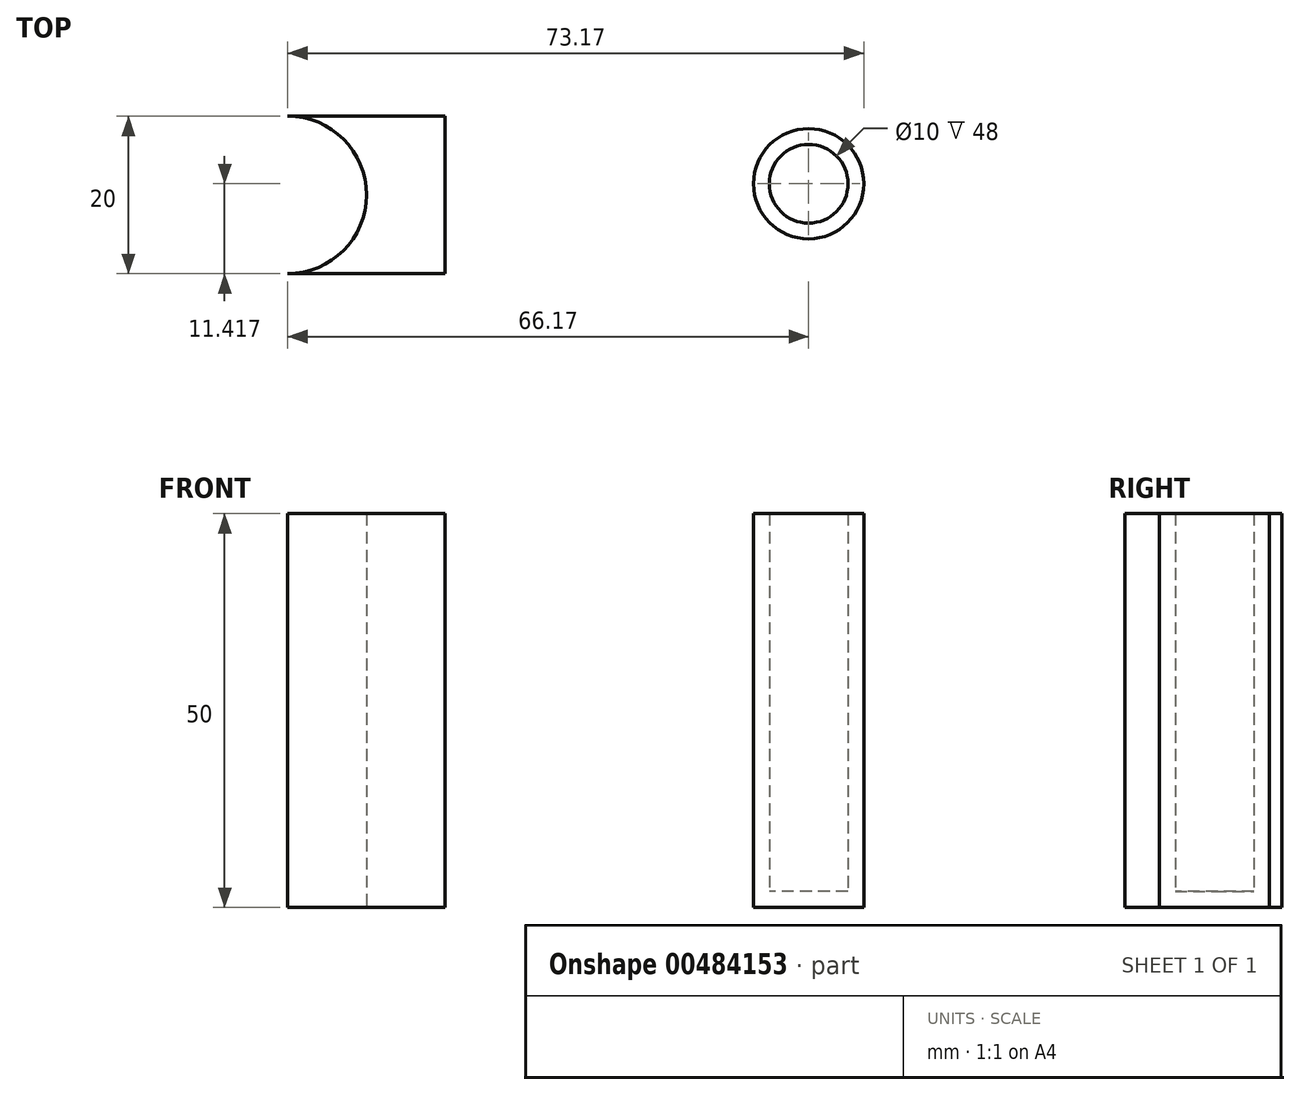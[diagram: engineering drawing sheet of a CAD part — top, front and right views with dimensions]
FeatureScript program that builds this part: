
annotation { "Feature Type Name" : "Feature", "Feature Type Description" : "" }
export const myFeature = defineFeature(function(context is Context, id is Id, definition is map)
    precondition{}
    {
        {
            var Q0;
            Q0=qCreatedBy(makeId("Top.planeOp"),FACE);
            var sketch = newSketch(context, id + "F0", { "sketchPlane" : qUnion([Q0])});
            skLineSegment(sketch, "E0.bottom", {"start": v(-19.05, 1.57) * mm, "end": v(0.95, 1.57) * mm});
            skLineSegment(sketch, "E0.top", {"start": v(-19.05, -18.43) * mm, "end": v(0.95, -18.43) * mm});
            skLineSegment(sketch, "E0.left", {"start": v(-19.05, 1.57) * mm, "end": v(-19.05, -18.43) * mm});
            skLineSegment(sketch, "E0.right", {"start": v(0.95, 1.57) * mm, "end": v(0.95, -18.43) * mm});
            skArc(sketch, "E1", {"start": v(-19.05, -18.43) * mm, "mid": v(-9.05, -8.43) * mm, "end": v(-19.05, 1.57) * mm});
            skCircle(sketch, "E2", {"center": v(47.12, -7.01) * mm, "radius": 7 * mm});
            skSolve(sketch);
        }
        {
            var Q0;
            Q0=makeQuery(id+"F0.imprint","IMPRINT",FACE,{"disambiguationData":[TD([[makeQuery(id+"F0.imprint","IMPRINT",EDGE,{"derivedFrom":sQuery(id+"F0.wireOp",EDGE,"E0.bottom")}),-1.0]])]});
            extrude(context, id + "F1", {"entities" : qUnion([Q0]), "depth" : 50 * mm, "offsetDistance" : 25 * mm});
        }
        {
            var Q0;
            Q0=makeQuery(id+"F0.imprint","IMPRINT",FACE,{"disambiguationData":[TD([[makeQuery(id+"F0.imprint","IMPRINT",EDGE,{"derivedFrom":sQuery(id+"F0.wireOp",EDGE,"E2")}),1.0]])]});
            extrude(context, id + "F2", {"entities" : qUnion([Q0]), "depth" : 50 * mm, "offsetDistance" : 25 * mm});
        }
        {
            var Q0;
            Q0=makeQuery(id+"F2.opExtrude","CAP_FACE",FACE,{"disambiguationData":[OSD([sQuery(id+"F0.wireOp",EDGE,"E2")])],"isStart":false});
            shell(context, id + "F3", {"entities" : qUnion([Q0]), "thickness" : 2 * mm});
        }
    });
